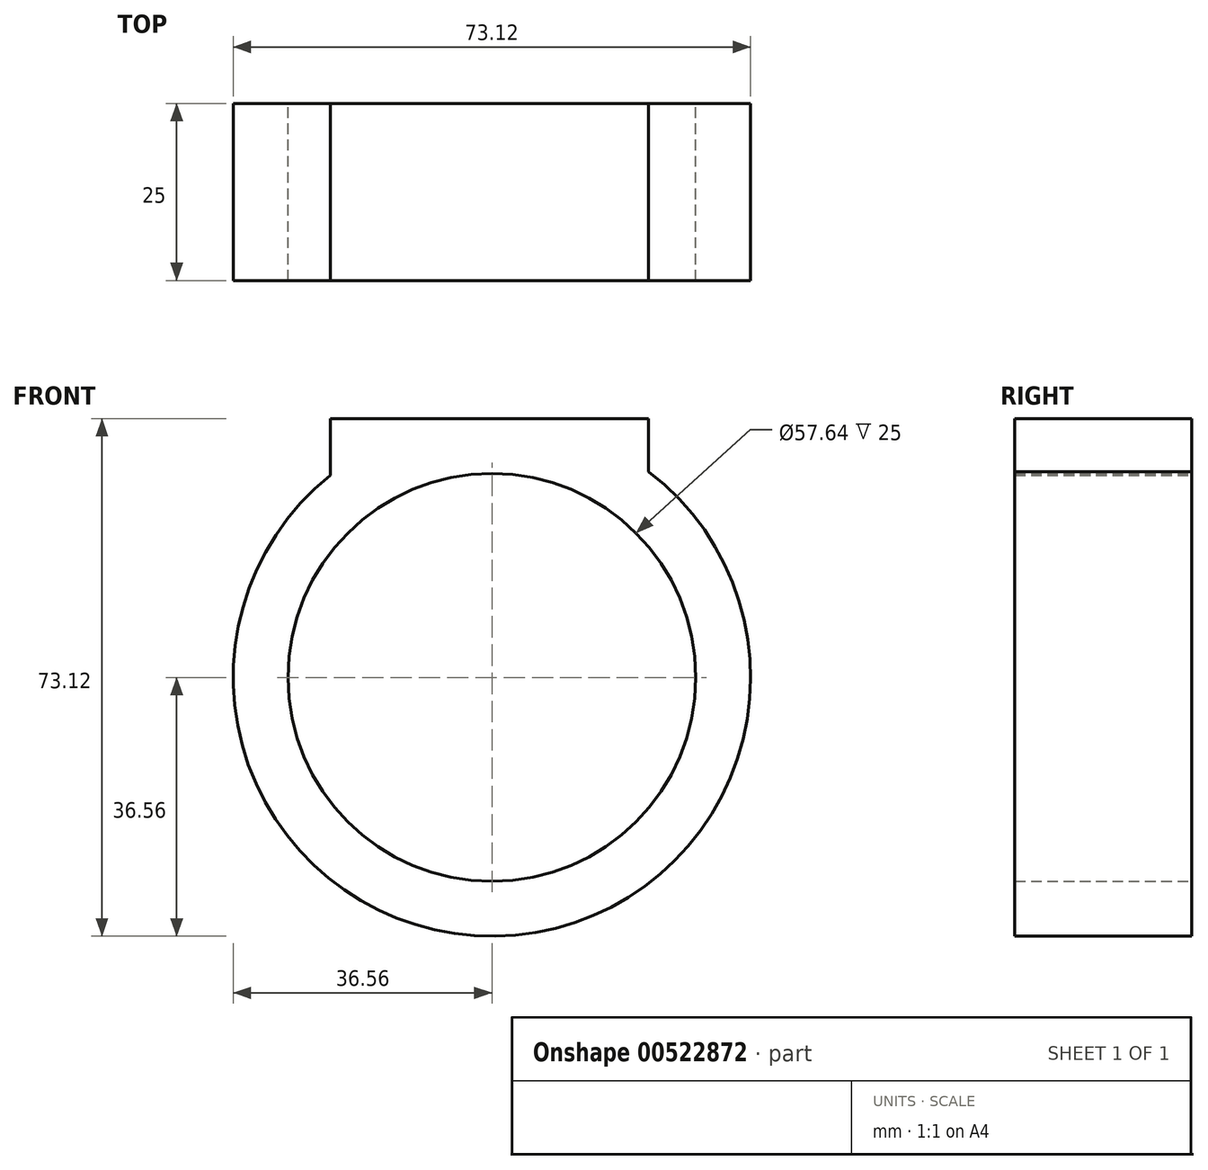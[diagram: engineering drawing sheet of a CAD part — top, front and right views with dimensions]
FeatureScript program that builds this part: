
annotation { "Feature Type Name" : "Feature", "Feature Type Description" : "" }
export const myFeature = defineFeature(function(context is Context, id is Id, definition is map)
    precondition{}
    {
        {
            var Q0;
            Q0=qCreatedBy(makeId("Front.planeOp"),FACE);
            var sketch = newSketch(context, id + "F0", { "sketchPlane" : qUnion([Q0])});
            skLineSegment(sketch, "E0.bottom", {"start": v(-22.85, 36.56) * mm, "end": v(22.15, 36.56) * mm});
            skLineSegment(sketch, "E0.left", {"start": v(-22.85, 36.56) * mm, "end": v(-22.85, 28.54) * mm});
            skLineSegment(sketch, "E0.right", {"start": v(22.15, 36.56) * mm, "end": v(22.15, 29.1) * mm});
            skPoint(sketch, "E0.middle", {"position": v(0, 0) * mm});
            skArc(sketch, "E1", {"start": v(-22.85, 28.54) * mm, "mid": v(0.45, -36.56) * mm, "end": v(22.15, 29.1) * mm});
            skCircle(sketch, "E2", {"center": v(0, 0) * mm, "radius": 28.82 * mm});
            skSolve(sketch);
        }
        {
            var Q0;
            Q0 = qSketchRegion(id + "F0", true);
            extrude(context, id + "F1", {"entities" : qUnion([Q0]), "depth" : 25 * mm, "offsetDistance" : 25 * mm});
        }
    });
